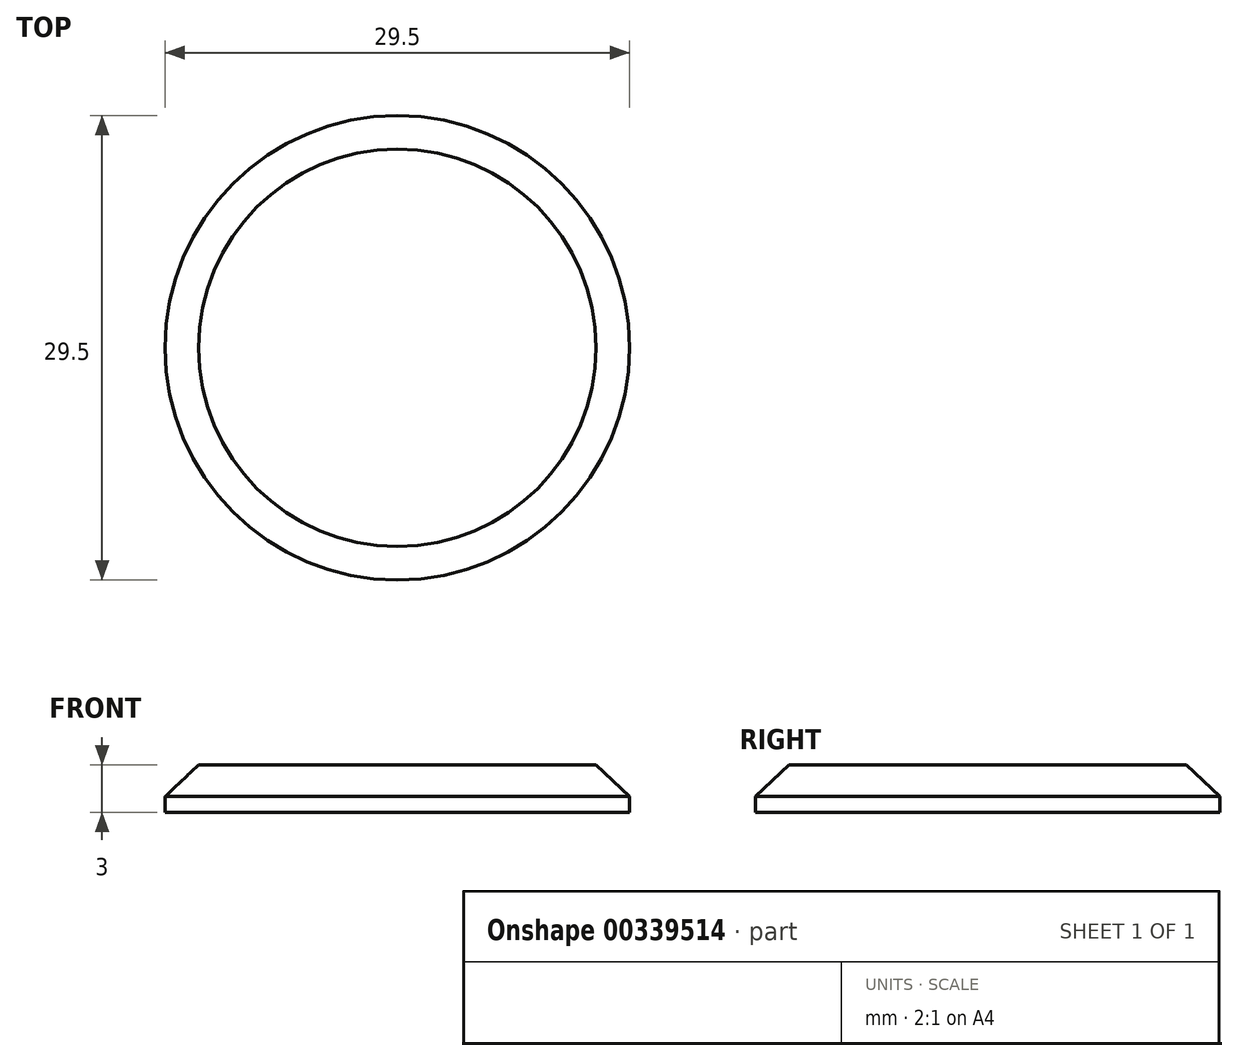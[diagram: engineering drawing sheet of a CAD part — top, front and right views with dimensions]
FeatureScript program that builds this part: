
annotation { "Feature Type Name" : "Feature", "Feature Type Description" : "" }
export const myFeature = defineFeature(function(context is Context, id is Id, definition is map)
    precondition{}
    {
        {
            var Q0;
            Q0=qCreatedBy(makeId("Right.planeOp"),FACE);
            var sketch = newSketch(context, id + "F0", { "sketchPlane" : qUnion([Q0])});
            skLineSegment(sketch, "E0", {"start": v(0, 0) * mm, "end": v(3.75, 0) * mm});
            skLineSegment(sketch, "E1", {"start": v(3.75, 0) * mm, "end": v(3.75, 64) * mm});
            skLineSegment(sketch, "E2", {"start": v(3.75, 64) * mm, "end": v(3.25, 64) * mm});
            skLineSegment(sketch, "E3", {"start": v(3.25, 64) * mm, "end": v(3.25, 65) * mm});
            skLineSegment(sketch, "E4", {"start": v(3.25, 65) * mm, "end": v(3.75, 65) * mm});
            skLineSegment(sketch, "E5", {"start": v(3.75, 65) * mm, "end": v(3.75, 70) * mm});
            skLineSegment(sketch, "E6", {"start": v(3.75, 70) * mm, "end": v(0, 70) * mm});
            skLineSegment(sketch, "E7", {"start": v(0, 70) * mm, "end": v(0, 0) * mm, "construction": true});
            skSolve(sketch);
        }
        {
            var Q0;
            Q0=sQuery(id+"F0.wireOp",EDGE,"E5");
            var Q1;
            Q1=sQuery(id+"F0.wireOp",EDGE,"E6");
            var Q2;
            Q2=sQuery(id+"F0.wireOp",EDGE,"E3");
            var Q3;
            Q3=sQuery(id+"F0.wireOp",EDGE,"E2");
            var Q4;
            Q4=sQuery(id+"F0.wireOp",EDGE,"E4");
            var Q5;
            Q5=sQuery(id+"F0.wireOp",EDGE,"E1");
            var Q6;
            Q6=sQuery(id+"F0.wireOp",EDGE,"E0");
            var Q7;
            Q7=sQuery(id+"F0.wireOp",EDGE,"E7");
            revolve(context, id + "F1", {"bodyType" : ExtendedToolBodyType.SURFACE, "surfaceEntities" : qUnion([Q0, Q1, Q2, Q3, Q4, Q5, Q6]), "axis" : qUnion([Q7]), "revolveType" : RevolveType.FULL});
        }
        {
            var Q0;
            Q0=makeQuery(id+"F1.opRevolve","SWEPT_FACE",FACE,{"disambiguationData":[OSD([sQuery(id+"F0.wireOp",EDGE,"E0")])]});
            cPlane(context, id + "F2", {"entities" : qUnion([Q0]), "cplaneType" : CPlaneType.OFFSET, "offset" : 15 * mm, "width" : 150 * mm, "height" : 150 * mm});
        }
        {
            var Q0;
            Q0=qCreatedBy(id+"F2.planeOp",FACE);
            var sketch = newSketch(context, id + "F3", { "sketchPlane" : qUnion([Q0])});
            skCircle(sketch, "E8", {"center": v(0, 0) * mm, "radius": 14.75 * mm});
            skSolve(sketch);
        }
        {
            var Q0;
            Q0 = qSketchRegion(id + "F3", true);
            extrude(context, id + "F4", {"entities" : qUnion([Q0]), "depth" : 1 * mm});
        }
        {
            var Q0;
            Q0=qCreatedBy(makeId("Right.planeOp"),FACE);
            var sketch = newSketch(context, id + "F5", { "sketchPlane" : qUnion([Q0])});
            skFitSpline(sketch, "E9.MirrorCS", {"points": [v(-3.75, 0) * mm, v(-5.04, -9.03) * mm, v(-12.63, -13) * mm], "startDerivative": vector(-0.97, -41.07) * mm, "endDerivative": vector(-36.74, -7.63) * mm});
            skLineSegment(sketch, "E10", {"start": v(0, 0) * mm, "end": v(0, -13) * mm, "construction": true});
            skLineSegment(sketch, "E11", {"start": v(0, 0) * mm, "end": v(-3.75, 0) * mm});
            skLineSegment(sketch, "E12", {"start": v(0, -13) * mm, "end": v(-12.63, -13) * mm});
            skSolve(sketch);
        }
        {
            var Q0;
            Q0=makeQuery(id+"F3.imprint","IMPRINT",FACE,{"disambiguationData":[TD([[makeQuery(id+"F3.imprint","IMPRINT",EDGE,{"derivedFrom":sQuery(id+"F3.wireOp",EDGE,"E8")}),1.0]])]});
            cPlane(context, id + "F6", {"entities" : qUnion([Q0]), "cplaneType" : CPlaneType.OFFSET, "offset" : 2 * mm, "oppositeDirection" : true, "width" : 150 * mm, "height" : 150 * mm});
        }
        {
            var Q0;
            Q0=qCreatedBy(id+"F6.planeOp",FACE);
            var sketch = newSketch(context, id + "F7", { "sketchPlane" : qUnion([Q0])});
            skCircle(sketch, "E13", {"center": v(0, 0) * mm, "radius": 12.62 * mm});
            skSolve(sketch);
        }
        {
            var Q1;
            Q1=makeQuery(id+"F3.imprint","IMPRINT",FACE,{"disambiguationData":[TD([[makeQuery(id+"F3.imprint","IMPRINT",EDGE,{"derivedFrom":sQuery(id+"F3.wireOp",EDGE,"E8")}),1.0]])]});
            var Q2;
            Q2=makeQuery(id+"F7.imprint","IMPRINT",FACE,{"disambiguationData":[TD([[makeQuery(id+"F7.imprint","IMPRINT",EDGE,{"derivedFrom":sQuery(id+"F7.wireOp",EDGE,"E13")}),1.0]])]});
            loft(context, id + "F8", {"operationType" : NewBodyOperationType.ADD, "sheetProfilesArray" : [{ "sheetProfileEntities" : qUnion([Q1]) }, { "sheetProfileEntities" : qUnion([Q2]) }]});
        }
        {
            var Q0;
            Q0=sQuery(id+"F5.wireOp",EDGE,"E9.MirrorCS");
            var Q1;
            Q1=sQuery(id+"F5.wireOp",EDGE,"E11");
            var Q2;
            Q2=sQuery(id+"F5.wireOp",EDGE,"E12");
            var Q3;
            Q3=sQuery(id+"F5.wireOp",EDGE,"E10");
            revolve(context, id + "F9", {"bodyType" : ExtendedToolBodyType.SURFACE, "surfaceEntities" : qUnion([Q0, Q1, Q2]), "axis" : qUnion([Q3]), "revolveType" : RevolveType.FULL});
        }
    });
